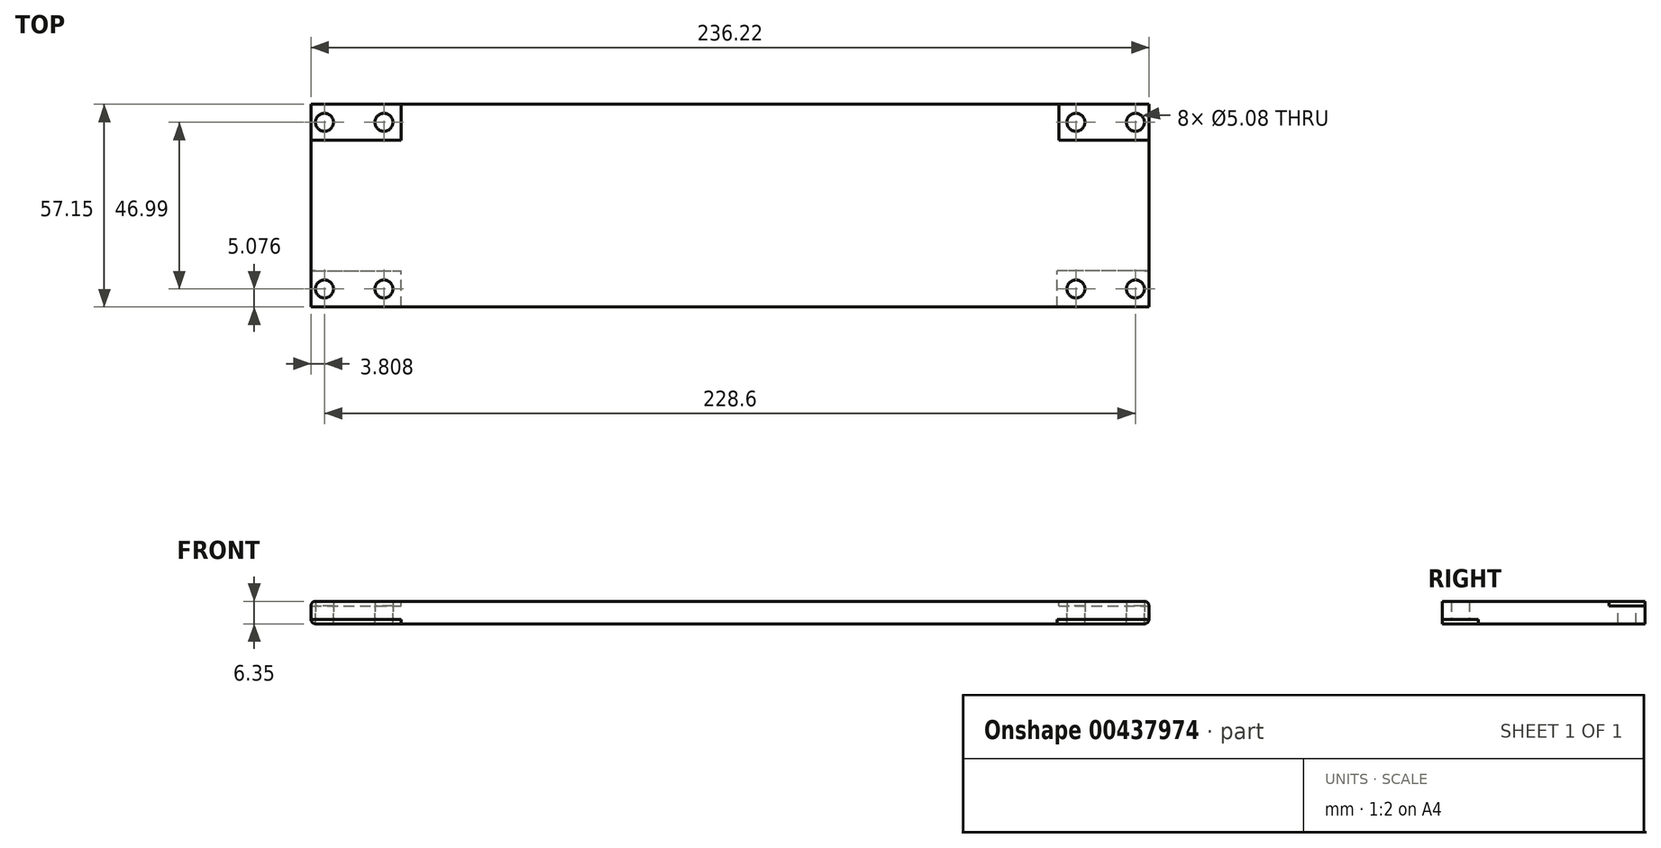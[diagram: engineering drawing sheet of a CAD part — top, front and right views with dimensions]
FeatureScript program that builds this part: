
annotation { "Feature Type Name" : "Feature", "Feature Type Description" : "" }
export const myFeature = defineFeature(function(context is Context, id is Id, definition is map)
    precondition{}
    {
        {
            var Q0;
            Q0=qCreatedBy(makeId("Top.planeOp"),FACE);
            var sketch = newSketch(context, id + "F0", { "sketchPlane" : qUnion([Q0])});
            skLineSegment(sketch, "E0.bottom", {"start": v(-101.64, 5.54) * mm, "end": v(-53.38, 5.54) * mm});
            skLineSegment(sketch, "E0.top", {"start": v(-101.64, -51.61) * mm, "end": v(-53.38, -51.61) * mm});
            skLineSegment(sketch, "E0.left", {"start": v(-101.64, 5.54) * mm, "end": v(-101.64, -51.61) * mm});
            skLineSegment(sketch, "E0.right", {"start": v(134.58, 5.54) * mm, "end": v(134.58, -51.61) * mm});
            skLineSegment(sketch, "E1.top", {"start": v(-53.38, -51.61) * mm, "end": v(86.32, -51.61) * mm});
            skLineSegment(sketch, "E1.left", {"start": v(-53.38, -51.61) * mm, "end": v(-53.38, -51.61) * mm});
            skLineSegment(sketch, "E1.right", {"start": v(86.32, -51.61) * mm, "end": v(86.32, -51.61) * mm});
            skPoint(sketch, "E2.oppositeSnap0", {"position": v(86.32, -55.42) * mm});
            skLineSegment(sketch, "E2.top", {"start": v(-53.38, 5.54) * mm, "end": v(86.32, 5.54) * mm});
            skLineSegment(sketch, "E2.left", {"start": v(-53.38, 5.54) * mm, "end": v(-53.38, 5.54) * mm});
            skLineSegment(sketch, "E2.right", {"start": v(86.32, 5.54) * mm, "end": v(86.32, 5.54) * mm});
            skLineSegment(sketch, "E3.trimOffspring", {"start": v(86.32, 5.54) * mm, "end": v(134.58, 5.54) * mm});
            skLineSegment(sketch, "E4.trimOffspring", {"start": v(86.32, -51.61) * mm, "end": v(134.58, -51.61) * mm});
            skSolve(sketch);
        }
        {
            var Q0;
            Q0=qSketchRegion(id+"F0",true);
            extrude(context, id + "F1", {"entities" : qUnion([Q0]), "depth" : 6.35 * mm});
        }
        {
            var Q0;
            Q0=makeQuery(id+"F1.opExtrude","CAP_FACE",FACE,{"disambiguationData":[OSD([sQuery(id+"F0.wireOp",EDGE,"E0.bottom"),sQuery(id+"F0.wireOp",EDGE,"E0.top"),sQuery(id+"F0.wireOp",EDGE,"E0.left"),sQuery(id+"F0.wireOp",EDGE,"E0.right"),sQuery(id+"F0.wireOp",EDGE,"E1.top"),sQuery(id+"F0.wireOp",EDGE,"E1.left"),sQuery(id+"F0.wireOp",EDGE,"E1.right"),sQuery(id+"F0.wireOp",EDGE,"E2.top"),sQuery(id+"F0.wireOp",EDGE,"E3.trimOffspring"),sQuery(id+"F0.wireOp",EDGE,"E4.trimOffspring")])],"isStart":false});
            var sketch = newSketch(context, id + "F2", { "sketchPlane" : qUnion([Q0])});
            skLineSegment(sketch, "E5.bottom", {"start": v(-101.64, 5.54) * mm, "end": v(-76.24, 5.54) * mm});
            skLineSegment(sketch, "E5.top", {"start": v(-101.64, -4.62) * mm, "end": v(-76.24, -4.62) * mm});
            skLineSegment(sketch, "E5.left", {"start": v(-101.64, 5.54) * mm, "end": v(-101.64, -4.62) * mm});
            skLineSegment(sketch, "E5.right", {"start": v(-76.24, 5.54) * mm, "end": v(-76.24, -4.62) * mm});
            skLineSegment(sketch, "E6.bottom", {"start": v(134.58, 5.54) * mm, "end": v(109.18, 5.54) * mm});
            skLineSegment(sketch, "E6.top", {"start": v(134.58, -4.62) * mm, "end": v(109.18, -4.62) * mm});
            skLineSegment(sketch, "E6.left", {"start": v(134.58, 5.54) * mm, "end": v(134.58, -4.62) * mm});
            skLineSegment(sketch, "E6.right", {"start": v(109.18, 5.54) * mm, "end": v(109.18, -4.62) * mm});
            skSolve(sketch);
        }
        {
            var Q0;
            Q0=qSketchRegion(id+"F2",true);
            extrude(context, id + "F3", {"entities" : qUnion([Q0]), "operationType" : NewBodyOperationType.REMOVE, "oppositeDirection" : true, "depth" : 1.27 * mm});
        }
        {
            var Q0;
            Q0=makeQuery(id+"F3.boolean.opBoolean","COPY",FACE,{"derivedFrom":makeQuery(id+"F3.opExtrude","CAP_FACE",FACE,{"disambiguationData":[OSD([sQuery(id+"F2.wireOp",EDGE,"E5.bottom"),sQuery(id+"F2.wireOp",EDGE,"E5.top"),sQuery(id+"F2.wireOp",EDGE,"E5.left"),sQuery(id+"F2.wireOp",EDGE,"E5.right")])],"isStart":false})});
            var sketch = newSketch(context, id + "F4", { "sketchPlane" : qUnion([Q0])});
            skCircle(sketch, "E7", {"center": v(-97.83, 0.46) * mm, "radius": 2.54 * mm});
            skPoint(sketch, "E7.centerSnap0", {"position": v(-101.64, 0.46) * mm});
            skCircle(sketch, "E8", {"center": v(-81.07, 0.46) * mm, "radius": 2.54 * mm});
            skSolve(sketch);
        }
        {
            var Q0;
            Q0=qSketchRegion(id+"F4",true);
            extrude(context, id + "F5", {"entities" : qUnion([Q0]), "operationType" : NewBodyOperationType.REMOVE, "oppositeDirection" : true, "depth" : 25.4 * mm});
        }
        {
            var Q0;
            Q0=makeQuery(id+"F3.boolean.opBoolean","COPY",FACE,{"derivedFrom":makeQuery(id+"F3.opExtrude","CAP_FACE",FACE,{"disambiguationData":[OSD([sQuery(id+"F2.wireOp",EDGE,"E6.bottom"),sQuery(id+"F2.wireOp",EDGE,"E6.top"),sQuery(id+"F2.wireOp",EDGE,"E6.left"),sQuery(id+"F2.wireOp",EDGE,"E6.right")])],"isStart":false})});
            var sketch = newSketch(context, id + "F6", { "sketchPlane" : qUnion([Q0])});
            skCircle(sketch, "E9", {"center": v(130.77, 0.46) * mm, "radius": 2.54 * mm});
            skPoint(sketch, "E9.centerSnap0", {"position": v(134.58, 0.46) * mm});
            skCircle(sketch, "E10", {"center": v(114, 0.46) * mm, "radius": 2.54 * mm});
            skSolve(sketch);
        }
        {
            var Q0;
            Q0=qSketchRegion(id+"F6",true);
            extrude(context, id + "F7", {"entities" : qUnion([Q0]), "operationType" : NewBodyOperationType.REMOVE, "oppositeDirection" : true, "depth" : 25.4 * mm});
        }
        {
            var Q0;
            Q0=makeQuery(id+"F1.opExtrude","CAP_FACE",FACE,{"disambiguationData":[OSD([sQuery(id+"F0.wireOp",EDGE,"E0.bottom"),sQuery(id+"F0.wireOp",EDGE,"E0.top"),sQuery(id+"F0.wireOp",EDGE,"E0.left"),sQuery(id+"F0.wireOp",EDGE,"E0.right"),sQuery(id+"F0.wireOp",EDGE,"E1.top"),sQuery(id+"F0.wireOp",EDGE,"E2.top"),sQuery(id+"F0.wireOp",EDGE,"E3.trimOffspring"),sQuery(id+"F0.wireOp",EDGE,"E4.trimOffspring")])],"isStart":true});
            var sketch = newSketch(context, id + "F8", { "sketchPlane" : qUnion([Q0])});
            skLineSegment(sketch, "E11.bottom", {"start": v(-101.64, 51.61) * mm, "end": v(-76.24, 51.61) * mm});
            skLineSegment(sketch, "E11.top", {"start": v(-101.64, 41.45) * mm, "end": v(-76.24, 41.45) * mm});
            skLineSegment(sketch, "E11.left", {"start": v(-101.64, 51.61) * mm, "end": v(-101.64, 41.45) * mm});
            skLineSegment(sketch, "E11.right", {"start": v(-76.24, 51.61) * mm, "end": v(-76.24, 41.45) * mm});
            skLineSegment(sketch, "E12.bottom", {"start": v(134.58, 51.61) * mm, "end": v(108.63, 51.61) * mm});
            skLineSegment(sketch, "E12.top", {"start": v(134.58, 41.45) * mm, "end": v(108.63, 41.45) * mm});
            skLineSegment(sketch, "E12.left", {"start": v(134.58, 51.61) * mm, "end": v(134.58, 41.45) * mm});
            skLineSegment(sketch, "E12.right", {"start": v(108.63, 51.61) * mm, "end": v(108.63, 41.45) * mm});
            skSolve(sketch);
        }
        {
            var Q0;
            Q0=qSketchRegion(id+"F8",true);
            extrude(context, id + "F9", {"entities" : qUnion([Q0]), "operationType" : NewBodyOperationType.REMOVE, "oppositeDirection" : true, "depth" : 1.27 * mm});
        }
        {
            var Q0;
            Q0=makeQuery(id+"F9.boolean.opBoolean","COPY",FACE,{"derivedFrom":makeQuery(id+"F9.opExtrude","CAP_FACE",FACE,{"disambiguationData":[OSD([sQuery(id+"F8.wireOp",EDGE,"E11.bottom"),sQuery(id+"F8.wireOp",EDGE,"E11.top"),sQuery(id+"F8.wireOp",EDGE,"E11.left"),sQuery(id+"F8.wireOp",EDGE,"E11.right")])],"isStart":false})});
            var sketch = newSketch(context, id + "F10", { "sketchPlane" : qUnion([Q0])});
            skCircle(sketch, "E13", {"center": v(-97.83, 46.53) * mm, "radius": 2.54 * mm});
            skPoint(sketch, "E13.centerSnap0", {"position": v(-101.64, 46.53) * mm});
            skCircle(sketch, "E14", {"center": v(-81.07, 46.53) * mm, "radius": 2.54 * mm});
            skSolve(sketch);
        }
        {
            var Q0;
            Q0=qSketchRegion(id+"F10",true);
            extrude(context, id + "F11", {"entities" : qUnion([Q0]), "operationType" : NewBodyOperationType.REMOVE, "oppositeDirection" : true, "depth" : 25.4 * mm});
        }
        {
            var Q0;
            Q0=makeQuery(id+"F9.boolean.opBoolean","COPY",FACE,{"derivedFrom":makeQuery(id+"F9.opExtrude","CAP_FACE",FACE,{"disambiguationData":[OSD([sQuery(id+"F8.wireOp",EDGE,"E12.bottom"),sQuery(id+"F8.wireOp",EDGE,"E12.top"),sQuery(id+"F8.wireOp",EDGE,"E12.left"),sQuery(id+"F8.wireOp",EDGE,"E12.right")])],"isStart":false})});
            var sketch = newSketch(context, id + "F12", { "sketchPlane" : qUnion([Q0])});
            skCircle(sketch, "E15", {"center": v(114, 46.53) * mm, "radius": 2.54 * mm});
            skPoint(sketch, "E15.centerSnap0", {"position": v(108.63, 46.53) * mm});
            skCircle(sketch, "E16", {"center": v(130.77, 46.53) * mm, "radius": 2.54 * mm});
            skSolve(sketch);
        }
        {
            var Q0;
            Q0=qSketchRegion(id+"F12",true);
            extrude(context, id + "F13", {"entities" : qUnion([Q0]), "operationType" : NewBodyOperationType.REMOVE, "oppositeDirection" : true, "depth" : 25.4 * mm});
        }
        {
            var Q0;
            Q0=makeQuery(id+"F1.opExtrude","CAP_EDGE",EDGE,{"disambiguationData":[OSD([sQuery(id+"F0.wireOp",EDGE,"E0.right")])],"isStart":false});
            var Q1;
            Q1=makeQuery(id+"F1.opExtrude","CAP_EDGE",EDGE,{"disambiguationData":[OSD([sQuery(id+"F0.wireOp",EDGE,"E0.right")])],"isStart":true});
            var Q2;
            Q2=makeQuery(id+"F1.opExtrude","CAP_EDGE",EDGE,{"disambiguationData":[OSD([sQuery(id+"F0.wireOp",EDGE,"E0.left")])],"isStart":false});
            var Q3;
            Q3=makeQuery(id+"F1.opExtrude","CAP_EDGE",EDGE,{"disambiguationData":[OSD([sQuery(id+"F0.wireOp",EDGE,"E0.left")])],"isStart":true});
            fillet(context, id + "F14", {"entities" : qUnion([Q0, Q1, Q2, Q3]), "radius" : 1.27 * mm, "tangentPropagation" : true, "allowEdgeOverflow" : false});
        }
    });
